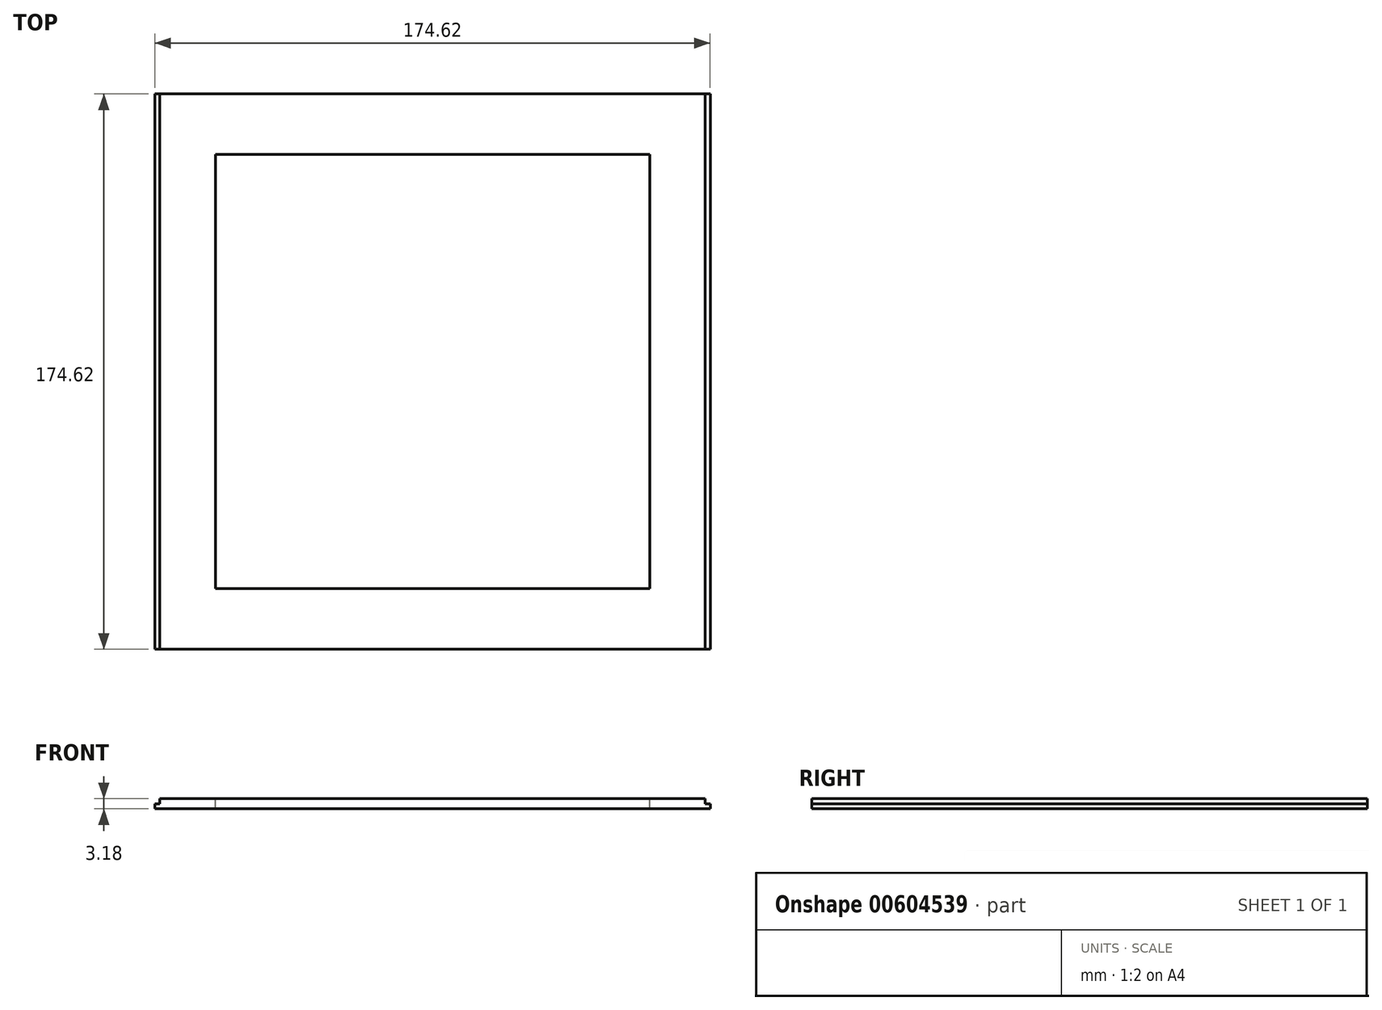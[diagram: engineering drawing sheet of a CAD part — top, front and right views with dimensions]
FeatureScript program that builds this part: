
annotation { "Feature Type Name" : "Feature", "Feature Type Description" : "" }
export const myFeature = defineFeature(function(context is Context, id is Id, definition is map)
    precondition{}
    {
        {
            var Q0;
            Q0=qCreatedBy(makeId("Top.planeOp"),FACE);
            var sketch = newSketch(context, id + "F0", { "sketchPlane" : qUnion([Q0])});
            skLineSegment(sketch, "E0.bottom", {"start": v(-87.31, 88.9) * mm, "end": v(87.31, 88.9) * mm});
            skLineSegment(sketch, "E0.top", {"start": v(-87.31, -85.73) * mm, "end": v(87.31, -85.73) * mm});
            skLineSegment(sketch, "E0.left", {"start": v(-87.31, 88.9) * mm, "end": v(-87.31, -85.73) * mm});
            skLineSegment(sketch, "E0.right", {"start": v(87.31, 88.9) * mm, "end": v(87.31, -85.73) * mm});
            skSolve(sketch);
        }
        {
            var Q0;
            Q0 = qSketchRegion(id + "F0", true);
            extrude(context, id + "F1", {"entities" : qUnion([Q0]), "depth" : 1.59 * mm, "offsetDistance" : 25.4 * mm});
        }
        {
            var Q0;
            Q0=makeQuery(id+"F1.opExtrude","CAP_FACE",FACE,{"disambiguationData":[OSD([sQuery(id+"F0.wireOp",EDGE,"E0.bottom"),sQuery(id+"F0.wireOp",EDGE,"E0.top"),sQuery(id+"F0.wireOp",EDGE,"E0.left"),sQuery(id+"F0.wireOp",EDGE,"E0.right"),sQuery(id+"F0.wireOp",EDGE,"YJX6Tguz-SMiq-THrU-rrjV-5SmgIMIBSolS.bottom"),sQuery(id+"F0.wireOp",EDGE,"YJX6Tguz-SMiq-THrU-rrjV-5SmgIMIBSolS.top"),sQuery(id+"F0.wireOp",EDGE,"YJX6Tguz-SMiq-THrU-rrjV-5SmgIMIBSolS.right"),sQuery(id+"F0.wireOp",EDGE,"TuNreRvB-bDLm-olZW-C4ir-dv5owGoYxZzy.bottom"),sQuery(id+"F0.wireOp",EDGE,"TuNreRvB-bDLm-olZW-C4ir-dv5owGoYxZzy.top"),sQuery(id+"F0.wireOp",EDGE,"TuNreRvB-bDLm-olZW-C4ir-dv5owGoYxZzy.right"),sQuery(id+"F0.wireOp",EDGE,"b73d8e7b-e983-4f92-b519-05f52655c729.filletArc"),sQuery(id+"F0.wireOp",EDGE,"cb04871c-d606-4326-9a4e-c13a588837c3.filletArc"),sQuery(id+"F0.wireOp",EDGE,"5633d6ac-3a86-4204-9a83-65c663d1d4e7.filletArc"),sQuery(id+"F0.wireOp",EDGE,"6f0b9e86-70b3-49d7-aae0-e9cdc36ab12a.filletArc")])],"isStart":false});
            var sketch = newSketch(context, id + "F2", { "sketchPlane" : qUnion([Q0])});
            skLineSegment(sketch, "E1.bottom", {"start": v(85.73, -85.73) * mm, "end": v(-85.72, -85.73) * mm});
            skLineSegment(sketch, "E1.top", {"start": v(85.72, 88.9) * mm, "end": v(-85.73, 88.9) * mm});
            skLineSegment(sketch, "E1.left", {"start": v(85.73, -85.73) * mm, "end": v(85.72, 88.9) * mm});
            skLineSegment(sketch, "E1.right", {"start": v(-85.72, -85.73) * mm, "end": v(-85.73, 88.9) * mm});
            skSolve(sketch);
        }
        {
            var Q0;
            Q0 = qSketchRegion(id + "F2", true);
            extrude(context, id + "F3", {"entities" : qUnion([Q0]), "operationType" : NewBodyOperationType.ADD, "depth" : 1.59 * mm, "offsetDistance" : 25.4 * mm});
        }
        {
            var Q0;
            Q0=makeQuery(id+"F3.opExtrude","CAP_FACE",FACE,{"disambiguationData":[OSD([sQuery(id+"F2.wireOp",EDGE,"E1.bottom"),sQuery(id+"F2.wireOp",EDGE,"E1.top"),sQuery(id+"F2.wireOp",EDGE,"E1.left"),sQuery(id+"F2.wireOp",EDGE,"E1.right")])],"isStart":false});
            var sketch = newSketch(context, id + "F4", { "sketchPlane" : qUnion([Q0])});
            skLineSegment(sketch, "E2.bottom", {"start": v(-68.26, 69.85) * mm, "end": v(68.26, 69.85) * mm});
            skLineSegment(sketch, "E2.top", {"start": v(-68.26, -66.68) * mm, "end": v(68.26, -66.68) * mm});
            skLineSegment(sketch, "E2.left", {"start": v(-68.26, 69.85) * mm, "end": v(-68.26, -66.68) * mm});
            skLineSegment(sketch, "E2.right", {"start": v(68.26, 69.85) * mm, "end": v(68.26, -66.68) * mm});
            skSolve(sketch);
        }
        {
            var Q0;
            Q0 = qSketchRegion(id + "F4", true);
            extrude(context, id + "F5", {"entities" : qUnion([Q0]), "operationType" : NewBodyOperationType.REMOVE, "oppositeDirection" : true, "depth" : 25.4 * mm, "offsetDistance" : 25.4 * mm});
        }
    });
